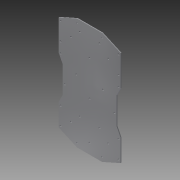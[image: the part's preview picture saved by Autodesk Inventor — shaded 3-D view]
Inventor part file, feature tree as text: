
AUTODESK INVENTOR PART (.ipt)
format: ipt  version: 2015 (Build 190159000, 159)  size: 163,840 bytes
history: native  units: mm
features: extrude x2, sketch x1
ambient origin geometry x8: Origin, YZ Plane, XZ Plane, XY Plane, X Axis, Y Axis, Z Axis, Center Point
bodies: Solid1 (feature_tree)
feature tree (3):
  sketch  "Sketch1"  dims[d0=4.0mm d1=4.0mm d2=4.0mm d3=4.0mm d4=4.0mm d5=4.0mm d6=4.0mm d7=4.0mm d8=4.0mm d9=4.0mm d10=4.0mm d11=4.0mm d12=4.0mm d13=4.0mm d14=4.0mm d15=4.0mm d16=4.0mm d17=4.0mm d18=4.0mm d19=4.0mm d20=4.0mm d21=4.0mm d22=4.0mm d23=4.0mm d24=4.0mm d25=2.0mm d26=0.0mm d28=3.0mm d29=3.0mm d31=3.0mm d32=3.0mm d33=2.0mm d34=0.0mm]
  extrude  "Extrusion1"  Depth=2.0mm
  extrude  "Extrusion2"  Depth=2.0mm
